# Revit family: HLC-B
name_source: partatom
category: Mechanical Equipment
units: mm (PartAtom-declared; Revit-internal decimal feet)

## family parameters
Always vertical = Yes
Cut with Voids When Loaded = No
Part Type = Normal
Room Calculation Point = No
Round Connector Dimension = Use Diameter
Shared = No
Work Plane-Based = No

## types (18) — shared parameters
0 = 0' - 0"
1" = 0' - 1"
1.5 = 0' - 1 1/2"
120 = 120.00°
2" = 0' - 2"
2' = 2' - 0"
4" = 0' - 4"
Manufacturer = Loren Cook Company
Model = HLC-B
ONE EIGTH = 0' - 0 1/8"
Type Comments = Hooded Low-Contour Downblast Centrifugal Exhaust Ventilator Roof Mounted/Belt Drive
URL = www.lorencook.com

## per-type parameters (varying)
| type | -(A/2) | -(C/2) | A | A/2 | B | B-C | B/2 | BASE/2 | BASE_OD | C | C-2 | C/2 | D | D-2 | D/2 | G | R_O | R_O/2 | T_SQ | T_SQ/2 |
| 100_HLC-B | -0' - 8 3/4" | -1' - 3 5/8" | 1' - 5 1/2" | 0' - 8 3/4" | 0' - 5 1/4" | -2' - 2" | 0' - 2 5/8" | 0' - 9 1/8" | 1' - 6 1/4" | 2' - 7 1/4" | 2' - 5 1/4" | 1' - 3 5/8" | 2' - 10 1/8" | -2' - 9 1/8" | 1' - 5 1/16" | 0' - 2" | 1' - 1 1/2" | 0' - 6 3/4" | 1' - 6" | 0' - 9" |
| 120_HLC-B | -0' - 9 13/16" | -1' - 5 3/8" | 1' - 7 5/8" | 0' - 9 13/16" | 0' - 5 7/8" | -2' - 4 7/8" | 0' - 2 15/16" | 0' - 10 1/8" | 1' - 8 1/4" | 2' - 10 3/4" | 2' - 8 3/4" | 1' - 5 3/8" | 2' - 11 1/8" | -2' - 10 1/8" | 1' - 5 9/16" | 0' - 2" | 1' - 3 1/2" | 0' - 7 3/4" | 1' - 8" | 0' - 10" |
| 135_HLC-B | -0' - 9 15/16" | -1' - 5 3/8" | 1' - 7 7/8" | 0' - 9 15/16" | 0' - 5 7/8" | -2' - 4 7/8" | 0' - 2 15/16" | 0' - 10 1/8" | 1' - 8 1/4" | 2' - 10 3/4" | 2' - 8 3/4" | 1' - 5 3/8" | 2' - 11 1/8" | -2' - 10 1/8" | 1' - 5 9/16" | 0' - 2" | 1' - 3 1/2" | 0' - 7 3/4" | 1' - 8" | 0' - 10" |
| 150_HLC-B | -0' - 10 5/8" | -1' - 8 1/16" | 1' - 9 1/4" | 0' - 10 5/8" | 0' - 7 3/8" | -2' - 8 3/4" | 0' - 3 11/16" | 1' - 0 1/8" | 2' - 0 1/4" | 3' - 4 1/8" | 3' - 2 1/8" | 1' - 8 1/16" | 3' - 6 1/8" | -3' - 5 1/8" | 1' - 9 1/16" | 0' - 2" | 1' - 7 1/2" | 0' - 9 3/4" | 2' - 0" | 1' - 0" |
| 165_HLC-B | -0' - 10 11/16" | -1' - 8 1/16" | 1' - 9 3/8" | 0' - 10 11/16" | 0' - 7 3/8" | -2' - 8 3/4" | 0' - 3 11/16" | 1' - 0 1/8" | 2' - 0 1/4" | 3' - 4 1/8" | 3' - 2 1/8" | 1' - 8 1/16" | 3' - 6 1/8" | -3' - 5 1/8" | 1' - 9 1/16" | 0' - 2" | 1' - 7 1/2" | 0' - 9 3/4" | 2' - 0" | 1' - 0" |
| 180_HLC-B | -1' - 1 1/8" | -1' - 9 15/16" | 2' - 2 1/4" | 1' - 1 1/8" | 0' - 8 1/4" | -2' - 11 5/8" | 0' - 4 1/8" | 1' - 3 1/8" | 2' - 6 1/4" | 3' - 7 7/8" | 3' - 5 7/8" | 1' - 9 15/16" | 3' - 11 1/8" | -3' - 10 1/8" | 1' - 11 9/16" | 0' - 3" | 2' - 1 1/2" | 1' - 0 3/4" | 2' - 6" | 1' - 3" |
| 195_HLC-B | -1' - 1 1/2" | -1' - 10" | 2' - 3" | 1' - 1 1/2" | 0' - 9 1/4" | -2' - 10 23/32" | 0' - 4 5/8" | 1' - 3 1/8" | 2' - 6 1/4" | 3' - 7 31/32" | 3' - 5 31/32" | 1' - 10" | 3' - 11 1/8" | -3' - 10 1/8" | 1' - 11 9/16" | 0' - 3" | 2' - 1 1/2" | 1' - 0 3/4" | 2' - 6" | 1' - 3" |
| 210_HLC-B | -1' - 2 1/8" | -1' - 11 5/16" | 2' - 4 1/4" | 1' - 2 1/8" | 0' - 9 1/4" | -3' - 1 3/8" | 0' - 4 5/8" | 1' - 3 1/8" | 2' - 6 1/4" | 3' - 10 5/8" | 3' - 8 5/8" | 1' - 11 5/16" | 4' - 1 1/8" | -4' - 0 1/8" | 2' - 0 9/16" | 0' - 3" | 2' - 1 1/2" | 1' - 0 3/4" | 2' - 6" | 1' - 3" |
| 225_HLC-B | -1' - 2 1/2" | -1' - 11 5/16" | 2' - 5" | 1' - 2 1/2" | 0' - 10" | -3' - 0 5/8" | 0' - 5" | 1' - 3 1/8" | 2' - 6 1/4" | 3' - 10 5/8" | 3' - 8 5/8" | 1' - 11 5/16" | 4' - 1 1/8" | -4' - 0 1/8" | 2' - 0 9/16" | 0' - 3" | 2' - 1 1/2" | 1' - 0 3/4" | 2' - 6" | 1' - 3" |
| 245_HLC-B | -1' - 2 13/16" | -1' - 11 5/16" | 2' - 5 5/8" | 1' - 2 13/16" | 0' - 10 5/8" | -3' - 0" | 0' - 5 5/16" | 1' - 3 1/8" | 2' - 6 1/4" | 3' - 10 5/8" | 3' - 8 5/8" | 1' - 11 5/16" | 4' - 1 1/8" | -4' - 0 1/8" | 2' - 0 9/16" | 0' - 3" | 2' - 1 1/2" | 1' - 0 3/4" | 2' - 6" | 1' - 3" |
| 270_HLC-B | -1' - 4 1/8" | -2' - 5 1/16" | 2' - 8 1/4" | 1' - 4 1/8" | 0' - 11" | -3' - 11 1/8" | 0' - 5 1/2" | 1' - 6 1/8" | 3' - 0 1/4" | 4' - 10 1/8" | 4' - 8 1/8" | 2' - 5 1/16" | 4' - 10 1/8" | -4' - 9 1/8" | 2' - 5 1/16" | 0' - 3" | 2' - 7 1/2" | 1' - 3 3/4" | 3' - 0" | 1' - 6" |
| 300_HLC-B | -1' - 4 11/16" | -2' - 5 1/16" | 2' - 9 3/8" | 1' - 4 11/16" | 1' - 0 1/8" | -3' - 10" | 0' - 6 1/16" | 1' - 6 1/8" | 3' - 0 1/4" | 4' - 10 1/8" | 4' - 8 1/8" | 2' - 5 1/16" | 4' - 10 1/8" | -4' - 9 1/8" | 2' - 5 1/16" | 0' - 3" | 2' - 7 1/2" | 1' - 3 3/4" | 3' - 0" | 1' - 6" |
| 330_HLC-B | -1' - 5 11/16" | -2' - 8 1/2" | 2' - 11 3/8" | 1' - 5 11/16" | 1' - 1 1/8" | -4' - 3 7/8" | 0' - 6 9/16" | 1' - 9 1/8" | 3' - 6 1/4" | 5' - 5" | 5' - 3" | 2' - 8 1/2" | 5' - 5" | -5' - 4" | 2' - 8 1/2" | 0' - 3" | 3' - 1 1/2" | 1' - 6 3/4" | 3' - 6" | 1' - 9" |
| 365_HLC-B | -1' - 6 1/8" | -2' - 8 1/2" | 3' - 0 1/4" | 1' - 6 1/8" | 1' - 2" | -4' - 3" | 0' - 7" | 1' - 9 1/8" | 3' - 6 1/4" | 5' - 5" | 5' - 3" | 2' - 8 1/2" | 5' - 5" | -5' - 4" | 2' - 8 1/2" | 0' - 3" | 3' - 1 1/2" | 1' - 6 3/4" | 3' - 6" | 1' - 9" |
| 402_HLC-B | -1' - 9 3/4" | -3' - 5 7/16" | 3' - 7 1/2" | 1' - 9 3/4" | 1' - 2 1/4" | -5' - 8 5/8" | 0' - 7 1/8" | 2' - 0 1/8" | 4' - 0 1/4" | 6' - 10 7/8" | 6' - 8 7/8" | 3' - 5 7/16" | 6' - 6 1/8" | -6' - 5 1/8" | 3' - 3 1/16" | 0' - 3" | 3' - 7 1/2" | 1' - 9 3/4" | 4' - 0" | 2' - 0" |
| 445_HLC-B | -1' - 10 3/8" | -3' - 5 7/16" | 3' - 8 3/4" | 1' - 10 3/8" | 1' - 4 1/2" | -5' - 6 3/8" | 0' - 8 1/4" | 2' - 3 1/8" | 4' - 6 1/4" | 6' - 10 7/8" | 6' - 8 7/8" | 3' - 5 7/16" | 6' - 6 1/8" | -6' - 5 1/8" | 3' - 3 1/16" | 0' - 3" | 4' - 1 1/2" | 2' - 0 3/4" | 4' - 6" | 2' - 3" |
| 490_HLC-B | -1' - 11 1/8" | -3' - 5 7/16" | 3' - 10 1/4" | 1' - 11 1/8" | 1' - 6" | -5' - 4 7/8" | 0' - 9" | 2' - 3 1/8" | 4' - 6 1/4" | 6' - 10 7/8" | 6' - 8 7/8" | 3' - 5 7/16" | 6' - 6 1/8" | -6' - 5 1/8" | 3' - 3 1/16" | 0' - 3" | 4' - 1 1/2" | 2' - 0 3/4" | 4' - 6" | 2' - 3" |
| 540_HLC-B | -1' - 10 15/16" | -4' - 0" | 3' - 9 7/8" | 1' - 10 15/16" | 1' - 1 5/8" | -6' - 10 3/8" | 0' - 6 13/16" | 2' - 9 1/8" | 5' - 6 1/4" | 8' - 0" | 7' - 10" | 4' - 0" | 8' - 2" | -8' - 1" | 4' - 1" | 0' - 3" | 5' - 1 1/2" | 2' - 6 3/4" | 5' - 6" | 2' - 9" |

## geometry (parser evidence)
native form markers: Sweep x1
no freeform markers — native parametric forms only
